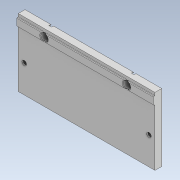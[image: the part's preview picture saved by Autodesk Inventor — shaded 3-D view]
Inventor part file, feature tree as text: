
AUTODESK INVENTOR PART (.ipt)
format: ipt  version: 2022.1 (Build 261234020, 234B)  size: 630,272 bytes
history: native  units: mm
features: sketch x13, reference x11, projected_geometry x9, extrude x8, hole x5, chamfer x3, other x3
ambient origin geometry x8: Origin, YZ Plane, XZ Plane, XY Plane, X Axis, Y Axis, Z Axis, Center Point
bodies: Volumenkörper1 (feature_tree)
feature tree (52):
  extrude  "Extrusion1"  Depth=0.4mm
  hole  "Bohrung1"  [1 undecoded]
  extrude  "Extrusion2"  Depth=6.0mm TaperAngle=0.0deg
  extrude  "Extrusion3"  Depth=0.1mm
  hole  "Bohrung2"  [1 undecoded]
  hole  "Bohrung3"  [1 undecoded]
  hole  "Bohrung4"  [1 undecoded]
  hole  "Bohrung5"  [1 undecoded]
  chamfer  "Fase1"  Distance=5.379mm
  chamfer  "Fase2"  Distance=5.8mm
  extrude  "Extrusion4"  Depth=2.9mm
  extrude  "Extrusion5"  Depth=2.9mm
  extrude  "Extrusion6"  Depth=1.0mm
  extrude  "Extrusion7"  Depth=1.0mm
  chamfer  "Fase3"  Distance=1.0mm Angle=45.0deg
  extrude  "Extrusion8"  Depth=1.0mm TaperAngle=45.0deg
  sketch  "Skizze1"  dims[d0=0.4mm d1=0.4mm]
  reference  "Referenz1"
  sketch  "Skizze2"  dims[d2=0.4mm d3=0.4mm]
  reference  "Referenz2"
  reference  "Referenz3"
  sketch  "Skizze3"  dims[d4=6.0mm d5=0.0mm]
  projected_geometry  "Projizierte Kontur1"
  sketch  "Skizze4"  dims[d6=3.34mm d7=6.0mm d8=4.7mm d9=5.0mm d10=90.0deg d11=8.0mm d12=20.594885mm d13=25.0mm d14=0.0mm]
  reference  "Referenz4"
  reference  "Referenz5"
  sketch  "Skizze6"  dims[d15=0.1mm d16=0.1mm]
  reference  "Referenz7"
  sketch  "Skizze7"  dims[d17=5.8mm d18=1.0mm]
  reference  "Referenz8"
  sketch  "Skizze8"  dims[d19=20.0mm d20=0.0mm]
  reference  "Referenz9"
  sketch  "Skizze9"  dims[d22=2.8mm d23=6.0mm d24=4.7mm d25=5.0mm d26=90.0deg d27=2.0mm d28=60.0deg]
  sketch  "Skizze10"  dims[d29=2.0mm d30=6.0mm d31=4.0mm d32=2.0mm d33=90.0deg d34=1.4mm d35=60.0deg d36=2.54mm]
  projected_geometry  "Projizierte Kontur2"
  sketch  "Skizze11"  dims[d37=6.659mm d38=8.75mm]
  projected_geometry  "Projizierte Kontur3"
  projected_geometry  "Projizierte Kontur4"
  sketch  "Skizze12"  dims[d39=2.54mm d40=2.54mm]
  projected_geometry  "Projizierte Kontur5"
  projected_geometry  "Projizierte Kontur6"
  projected_geometry  "Projizierte Kontur7"
  projected_geometry  "Projizierte Kontur8"
  sketch  "Skizze13"  dims[d41=6.15mm]
  projected_geometry  "Projizierte Kontur9"
  sketch  "Skizze14"  dims[d42=4.3mm d43=5.379mm d44=2.0mm d45=6.0mm d46=4.0mm d47=2.0mm d48=90.0deg d49=1.4mm d50=60.0deg d51=5.8mm d52=2.9mm d53=2.9mm d54=20.0mm d55=20.0mm d56=5.4mm d57=6.0mm d58=9.4mm d59=2.8mm d60=90.0deg d61=1.4mm d62=60.0deg d63=1.0mm d64=2.0mm d65=45.0deg d66=0.4mm d67=2.0mm d68=45.0deg d69=0.0mm d70=0.0mm d71=2.0mm d72=2.0mm d73=25.0mm d74=0.0mm d75=0.2mm d76=0.0mm d77=0.4mm d78=0.0mm d79=0.0mm d80=0.0mm d81=1.6mm d82=1.6mm d83=0.4mm d84=0.0mm d85=0.4mm d86=2.0mm d87=45.0deg d88=10.0mm d89=10.0mm d90=0.0mm d91=0.0mm d92=0.0mm d93=0.0mm d94=4.0mm d95=6.0mm d96=1.0mm d97=0.0mm]
  reference  "Referenz10"
  reference  "Referenz11"
  reference  "Referenz12"
  other  "Baugruppe18"
  other  "STM32_Klipper_Expander:1"
  other  "HFSB5-2020-240:1"
note: 5 required parameter values undecoded (feature->parameter linkage not recoverable at this tier; creation-order binding heuristic only, values carry confidence <= 0.55)
